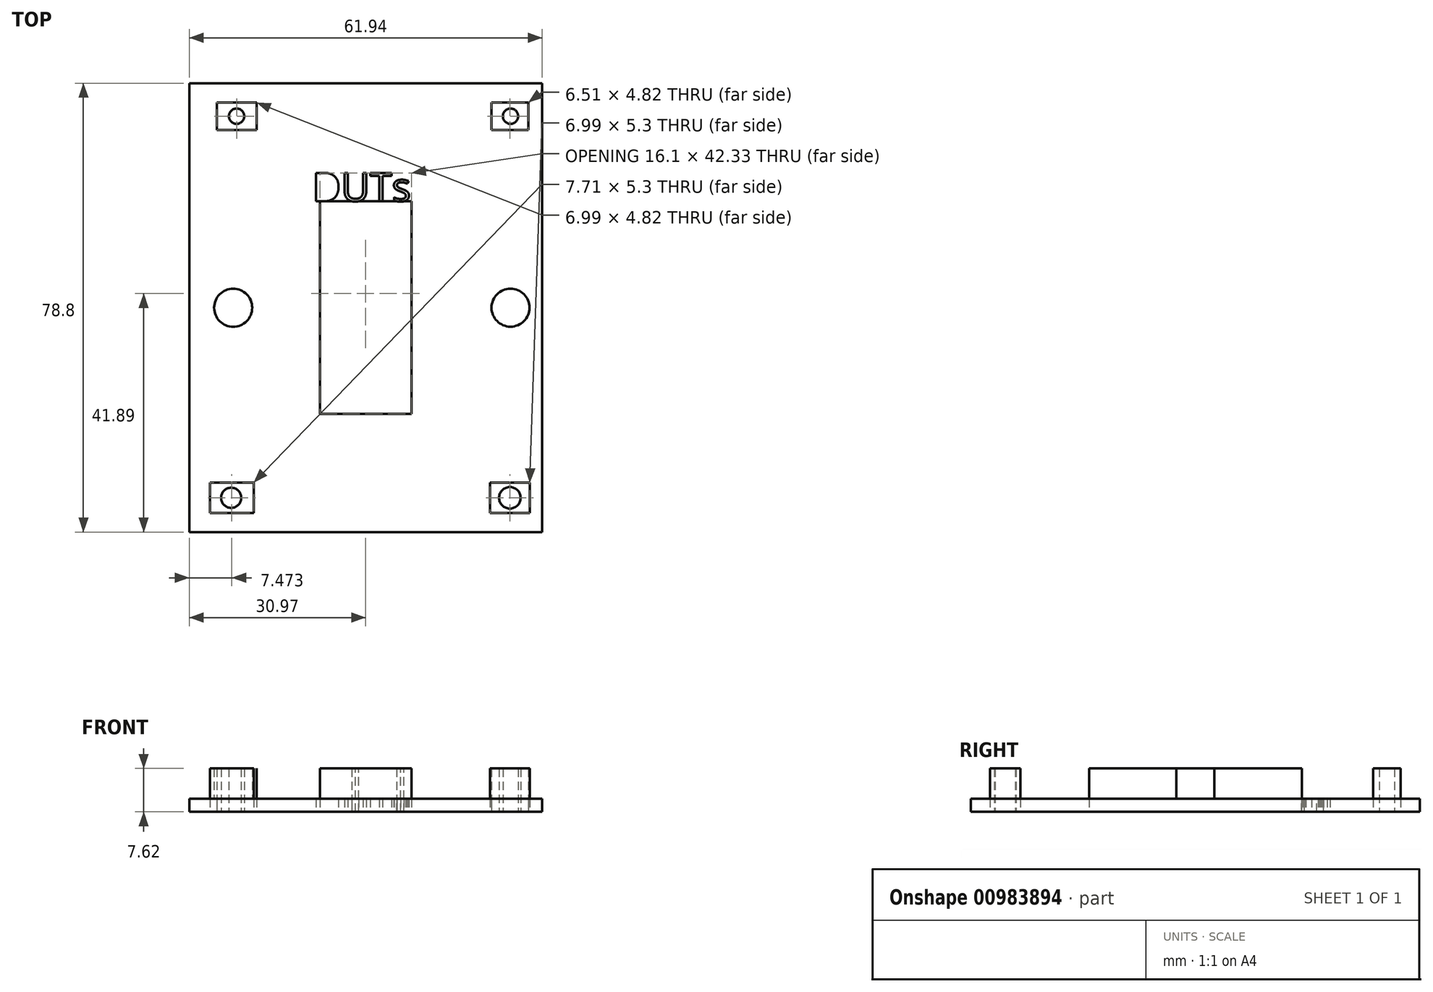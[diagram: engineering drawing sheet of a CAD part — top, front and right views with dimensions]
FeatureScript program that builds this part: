
annotation { "Feature Type Name" : "Feature", "Feature Type Description" : "" }
export const myFeature = defineFeature(function(context is Context, id is Id, definition is map)
    precondition{}
    {
        {
            var Q0;
            Q0=qCreatedBy(makeId("Top.planeOp"),FACE);
            var sketch = newSketch(context, id + "F0", { "sketchPlane" : qUnion([Q0])});
            skLineSegment(sketch, "E0.bottom", {"start": v(30.97, -39.4) * mm, "end": v(-30.97, -39.4) * mm});
            skLineSegment(sketch, "E0.top", {"start": v(30.97, 39.4) * mm, "end": v(-30.97, 39.4) * mm});
            skLineSegment(sketch, "E0.left", {"start": v(30.97, -39.4) * mm, "end": v(30.97, 39.4) * mm});
            skLineSegment(sketch, "E0.right", {"start": v(-30.97, -39.4) * mm, "end": v(-30.97, 39.4) * mm});
            skPoint(sketch, "E0.middle", {"position": v(0, 0) * mm});
            skLineSegment(sketch, "E1.bottom", {"start": v(-26.15, 36.03) * mm, "end": v(-19.16, 36.03) * mm});
            skLineSegment(sketch, "E1.top", {"start": v(-26.15, 31.2) * mm, "end": v(-19.16, 31.2) * mm});
            skLineSegment(sketch, "E1.left", {"start": v(-26.15, 36.03) * mm, "end": v(-26.15, 31.2) * mm});
            skLineSegment(sketch, "E1.right", {"start": v(-19.16, 36.03) * mm, "end": v(-19.16, 31.2) * mm});
            skLineSegment(sketch, "E2.bottom", {"start": v(22.05, 31.2) * mm, "end": v(28.56, 31.2) * mm});
            skLineSegment(sketch, "E2.top", {"start": v(22.05, 36.03) * mm, "end": v(28.56, 36.03) * mm});
            skLineSegment(sketch, "E2.left", {"start": v(22.05, 31.2) * mm, "end": v(22.05, 36.03) * mm});
            skLineSegment(sketch, "E2.right", {"start": v(28.56, 31.2) * mm, "end": v(28.56, 36.03) * mm});
            skLineSegment(sketch, "E3.bottom", {"start": v(8.05, 18.68) * mm, "end": v(-8.05, 18.68) * mm});
            skLineSegment(sketch, "E3.top", {"start": v(8.05, -18.68) * mm, "end": v(-8.05, -18.68) * mm});
            skLineSegment(sketch, "E3.left", {"start": v(8.05, 18.68) * mm, "end": v(8.05, -18.68) * mm});
            skLineSegment(sketch, "E3.right", {"start": v(-8.05, 18.68) * mm, "end": v(-8.05, -18.68) * mm});
            skLineSegment(sketch, "E4.bottom", {"start": v(-27.35, -36.03) * mm, "end": v(-19.64, -36.03) * mm});
            skLineSegment(sketch, "E4.top", {"start": v(-27.35, -30.73) * mm, "end": v(-19.64, -30.73) * mm});
            skLineSegment(sketch, "E4.left", {"start": v(-27.35, -36.03) * mm, "end": v(-27.35, -30.73) * mm});
            skLineSegment(sketch, "E4.right", {"start": v(-19.64, -36.03) * mm, "end": v(-19.64, -30.73) * mm});
            skLineSegment(sketch, "E5.bottom", {"start": v(21.8, -36.03) * mm, "end": v(28.8, -36.03) * mm});
            skLineSegment(sketch, "E5.top", {"start": v(21.8, -30.73) * mm, "end": v(28.8, -30.73) * mm});
            skLineSegment(sketch, "E5.left", {"start": v(21.8, -36.03) * mm, "end": v(21.8, -30.73) * mm});
            skLineSegment(sketch, "E5.right", {"start": v(28.8, -36.03) * mm, "end": v(28.8, -30.73) * mm});
            skCircle(sketch, "E6", {"center": v(-22.65, 33.62) * mm, "radius": 1.35 * mm});
            skPoint(sketch, "E6.centerSnap0", {"position": v(-26.15, 33.62) * mm});
            skPoint(sketch, "E6.centerSnap1", {"position": v(-22.65, 31.2) * mm});
            skCircle(sketch, "E7", {"center": v(25.42, 33.62) * mm, "radius": 1.35 * mm});
            skPoint(sketch, "E7.centerSnap0", {"position": v(-19.16, 33.62) * mm});
            skCircle(sketch, "E8", {"center": v(25.3, -33.38) * mm, "radius": 1.9 * mm});
            skPoint(sketch, "E8.centerSnap0", {"position": v(25.3, -36.03) * mm});
            skPoint(sketch, "E8.centerSnap1", {"position": v(21.8, -33.38) * mm});
            skCircle(sketch, "E9", {"center": v(-23.6, -33.38) * mm, "radius": 1.77 * mm});
            skPoint(sketch, "E9.centerSnap0", {"position": v(28.8, -33.38) * mm});
            skText(sketch, "E10", { "text": "DUTs", "fontName": "OpenSans-Regular.ttf"});
            skCircle(sketch, "E11", {"center": v(-23.26, 0) * mm, "radius": 3.34 * mm});
            skCircle(sketch, "E12", {"center": v(25.42, 0) * mm, "radius": 3.33 * mm});
            skPoint(sketch, "E12.centerSnap0", {"position": v(8.05, 0) * mm});
            const initialGuessF0  = {"E10": [-0.00942, 0.01868, 1, 0, 0.00502]};
            skSetInitialGuess(sketch, initialGuessF0);
            skSolve(sketch);
        }
        {
            var Q0;
            Q0=makeQuery(id+"F0.imprint","IMPRINT",FACE,{"disambiguationData":[TD([[makeQuery(id+"F0.imprint","IMPRINT",EDGE,{"derivedFrom":sQuery(id+"F0.wireOp",EDGE,"E4.bottom")}),1.0]])]});
            extrude(context, id + "F1", {"entities" : qUnion([Q0]), "depth" : 5.08 * mm, "offsetDistance" : 25.4 * mm});
        }
        {
            var Q0;
            Q0=makeQuery(id+"F0.imprint","IMPRINT",FACE,{"disambiguationData":[TD([[makeQuery(id+"F0.imprint","IMPRINT",EDGE,{"derivedFrom":sQuery(id+"F0.wireOp",EDGE,"E3.bottom")}),1.0]])]});
            var Q1;
            Q1=makeQuery(id+"F0.imprint","IMPRINT",FACE,{"disambiguationData":[TD([[makeQuery(id+"F0.imprint","IMPRINT",EDGE,{"derivedFrom":sQuery(id+"F0.wireOp",EDGE,"E1.bottom")}),-1.0]])]});
            var Q2;
            Q2=makeQuery(id+"F0.imprint","IMPRINT",FACE,{"disambiguationData":[TD([[makeQuery(id+"F0.imprint","IMPRINT",EDGE,{"derivedFrom":sQuery(id+"F0.wireOp",EDGE,"E2.bottom")}),1.0]])]});
            var Q3;
            Q3=makeQuery(id+"F0.imprint","IMPRINT",FACE,{"disambiguationData":[TD([[makeQuery(id+"F0.imprint","IMPRINT",EDGE,{"derivedFrom":sQuery(id+"F0.wireOp",EDGE,"E5.bottom")}),1.0]])]});
            extrude(context, id + "F2", {"entities" : qUnion([Q0, Q1, Q2, Q3]), "depth" : 5.08 * mm, "offsetDistance" : 25.4 * mm});
        }
        {
            var Q0;
            Q0=makeQuery(id+"F0.imprint","IMPRINT",FACE,{"disambiguationData":[TD([[makeQuery(id+"F0.imprint","IMPRINT",EDGE,{"derivedFrom":sQuery(id+"F0.wireOp",EDGE,"E0.bottom")}),-1.0]])]});
            extrude(context, id + "F3", {"entities" : qUnion([Q0]), "depth" : 2.31 * mm, "offsetDistance" : 25.4 * mm});
        }
        {
            var Q0;
            Q0=makeQuery(id+"F0.imprint","IMPRINT",FACE,{"disambiguationData":[TD([[makeQuery(id+"F0.imprint","IMPRINT",EDGE,{"derivedFrom":sQuery(id+"F0.wireOp",EDGE,"E12")}),1.0]])]});
            extrude(context, id + "F4", {"entities" : qUnion([Q0]), "operationType" : NewBodyOperationType.ADD, "depth" : 5.08 * mm, "offsetDistance" : 25.4 * mm});
        }
        {
            var Q0;
            Q0=makeQuery(id+"F0.imprint","IMPRINT",FACE,{"disambiguationData":[TD([[makeQuery(id+"F0.imprint","IMPRINT",EDGE,{"derivedFrom":sQuery(id+"F0.wireOp",EDGE,"E11")}),1.0]])]});
            extrude(context, id + "F5", {"entities" : qUnion([Q0]), "operationType" : NewBodyOperationType.ADD, "depth" : 5.08 * mm, "offsetDistance" : 25.4 * mm});
        }
        {
            var Q0;
            Q0=makeQuery(id+"F1.opExtrude","CAP_FACE",FACE,{"disambiguationData":[OSD([sQuery(id+"F0.wireOp",EDGE,"E4.bottom"),sQuery(id+"F0.wireOp",EDGE,"E4.top"),sQuery(id+"F0.wireOp",EDGE,"E4.left"),sQuery(id+"F0.wireOp",EDGE,"E4.right"),sQuery(id+"F0.wireOp",EDGE,"E9")])],"isStart":false});
            var Q1;
            Q1=makeQuery(id+"F2.opExtrude","CAP_FACE",FACE,{"disambiguationData":[OSD([sQuery(id+"F0.wireOp",EDGE,"E5.bottom"),sQuery(id+"F0.wireOp",EDGE,"E5.top"),sQuery(id+"F0.wireOp",EDGE,"E5.left"),sQuery(id+"F0.wireOp",EDGE,"E5.right"),sQuery(id+"F0.wireOp",EDGE,"E8")])],"isStart":false});
            var Q2;
            Q2=makeQuery(id+"F2.opExtrude","CAP_FACE",FACE,{"disambiguationData":[OSD([sQuery(id+"F0.wireOp",EDGE,"E1.bottom"),sQuery(id+"F0.wireOp",EDGE,"E1.top"),sQuery(id+"F0.wireOp",EDGE,"E1.left"),sQuery(id+"F0.wireOp",EDGE,"E1.right"),sQuery(id+"F0.wireOp",EDGE,"E6")])],"isStart":false});
            var Q3;
            Q3=makeQuery(id+"F2.opExtrude","CAP_FACE",FACE,{"disambiguationData":[OSD([sQuery(id+"F0.wireOp",EDGE,"E2.bottom"),sQuery(id+"F0.wireOp",EDGE,"E2.top"),sQuery(id+"F0.wireOp",EDGE,"E2.left"),sQuery(id+"F0.wireOp",EDGE,"E2.right"),sQuery(id+"F0.wireOp",EDGE,"E7")])],"isStart":false});
            var Q4;
            Q4=makeQuery(id+"F5.opExtrude","CAP_FACE",FACE,{"disambiguationData":[OSD([sQuery(id+"F0.wireOp",EDGE,"E11")])],"isStart":false});
            var Q5;
            Q5=makeQuery(id+"F4.opExtrude","CAP_FACE",FACE,{"disambiguationData":[OSD([sQuery(id+"F0.wireOp",EDGE,"E12")])],"isStart":false});
            extrude(context, id + "F6", {"entities" : qUnion([Q0, Q1, Q2, Q3, Q4, Q5]), "operationType" : NewBodyOperationType.ADD, "depth" : 2.54 * mm, "offsetDistance" : 25.4 * mm});
        }
        {
            var Q0;
            Q0=makeQuery(id+"F2.opExtrude","CAP_FACE",FACE,{"disambiguationData":[OSD([sQuery(id+"F0.wireOp",EDGE,"E3.bottom"),sQuery(id+"F0.wireOp",EDGE,"E3.top"),sQuery(id+"F0.wireOp",EDGE,"E3.left"),sQuery(id+"F0.wireOp",EDGE,"E3.right"),sQuery(id+"F0.wireOp",EDGE,"E10.sketch_text.stroke-2"),sQuery(id+"F0.wireOp",EDGE,"E10.sketch_text.stroke-16"),sQuery(id+"F0.wireOp",EDGE,"E10.sketch_text.stroke-17"),sQuery(id+"F0.wireOp",EDGE,"E10.sketch_text.stroke-28"),sQuery(id+"F0.wireOp",EDGE,"E10.sketch_text.stroke-37"),sQuery(id+"F0.wireOp",EDGE,"E10.sketch_text.stroke-38")])],"isStart":false});
            extrude(context, id + "F7", {"entities" : qUnion([Q0]), "operationType" : NewBodyOperationType.ADD, "depth" : 2.54 * mm, "offsetDistance" : 25.4 * mm});
        }
    });
